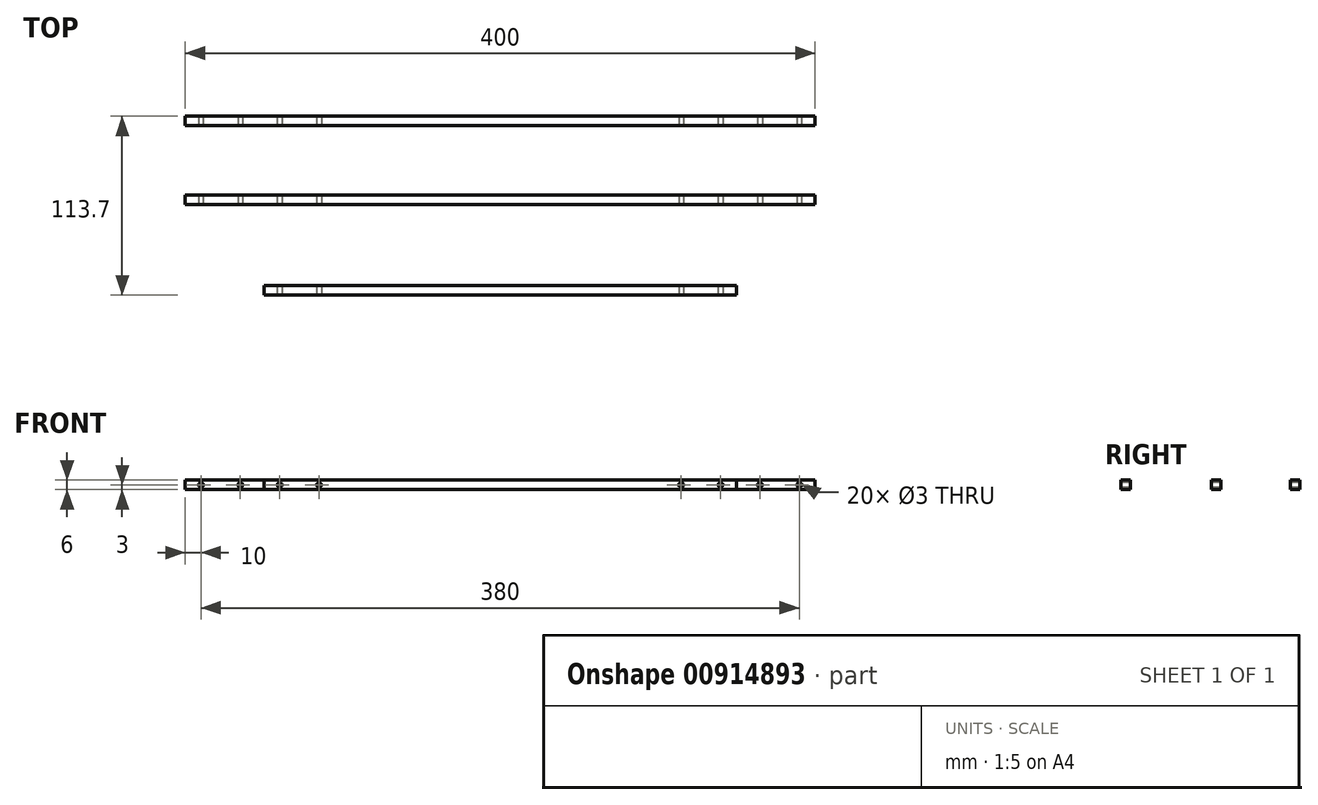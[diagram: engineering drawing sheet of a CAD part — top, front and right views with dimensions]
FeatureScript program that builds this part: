
annotation { "Feature Type Name" : "Feature", "Feature Type Description" : "" }
export const myFeature = defineFeature(function(context is Context, id is Id, definition is map)
    precondition{}
    {
        {
            var Q0;
            Q0=qCreatedBy(makeId("Top.planeOp"),FACE);
            var sketch = newSketch(context, id + "F0", { "sketchPlane" : qUnion([Q0])});
            skLineSegment(sketch, "E0.bottom", {"start": v(200, -3) * mm, "end": v(-200, -3) * mm});
            skLineSegment(sketch, "E0.top", {"start": v(200, 3) * mm, "end": v(-200, 3) * mm});
            skLineSegment(sketch, "E0.left", {"start": v(200, -3) * mm, "end": v(200, 3) * mm});
            skLineSegment(sketch, "E0.right", {"start": v(-200, -3) * mm, "end": v(-200, 3) * mm});
            skPoint(sketch, "E0.middle", {"position": v(0, 0) * mm});
            skLineSegment(sketch, "E1.bottom", {"start": v(150, -110.7) * mm, "end": v(-150, -110.7) * mm});
            skLineSegment(sketch, "E1.top", {"start": v(150, -104.7) * mm, "end": v(-150, -104.7) * mm});
            skLineSegment(sketch, "E1.left", {"start": v(150, -110.7) * mm, "end": v(150, -104.7) * mm});
            skLineSegment(sketch, "E1.right", {"start": v(-150, -110.7) * mm, "end": v(-150, -104.7) * mm});
            skPoint(sketch, "E1.middle", {"position": v(0, -107.7) * mm});
            skSolve(sketch);
        }
        {
            var Q0;
            Q0=makeQuery(id+"F0.imprint","IMPRINT",FACE,{"disambiguationData":[TD([[makeQuery(id+"F0.imprint","IMPRINT",EDGE,{"derivedFrom":sQuery(id+"F0.wireOp",EDGE,"E0.bottom")}),-1.0]])]});
            extrude(context, id + "F1", {"entities" : qUnion([Q0]), "depth" : 6 * mm, "offsetDistance" : 25 * mm});
        }
        {
            var Q0;
            Q0=qCreatedBy(makeId("Top.planeOp"),FACE);
            var sketch = newSketch(context, id + "F2", { "sketchPlane" : qUnion([Q0])});
            skLineSegment(sketch, "E2.bottom", {"start": v(200, -53) * mm, "end": v(-200, -53) * mm});
            skLineSegment(sketch, "E2.top", {"start": v(200, -47) * mm, "end": v(-200, -47) * mm});
            skLineSegment(sketch, "E2.left", {"start": v(200, -53) * mm, "end": v(200, -47) * mm});
            skLineSegment(sketch, "E2.right", {"start": v(-200, -53) * mm, "end": v(-200, -47) * mm});
            skPoint(sketch, "E2.middle", {"position": v(0, -50) * mm});
            skSolve(sketch);
        }
        {
            var Q0;
            Q0 = qSketchRegion(id + "F2", true);
            extrude(context, id + "F3", {"entities" : qUnion([Q0]), "depth" : 6 * mm, "offsetDistance" : 25 * mm});
        }
        {
            var Q0;
            Q0=makeQuery(id+"F1.opExtrude","SWEPT_FACE",FACE,{"disambiguationData":[OSD([sQuery(id+"F0.wireOp",EDGE,"E0.bottom")])]});
            var sketch = newSketch(context, id + "F4", { "sketchPlane" : qUnion([Q0])});
            skLineSegment(sketch, "E3", {"start": v(0, 24.85) * mm, "end": v(0, -23.8) * mm, "construction": true});
            skLineSegment(sketch, "E4", {"start": v(203.05, 3) * mm, "end": v(153.8, 3) * mm, "construction": true});
            skPoint(sketch, "E4.startSnap0", {"position": v(200, 3) * mm});
            skCircle(sketch, "E5", {"center": v(190, 3) * mm, "radius": 1.5 * mm});
            skCircle(sketch, "E6", {"center": v(165, 3) * mm, "radius": 1.5 * mm});
            skCircle(sketch, "E7.MirrorC", {"center": v(-190, 3) * mm, "radius": 1.5 * mm});
            skCircle(sketch, "E8.MirrorC", {"center": v(-165, 3) * mm, "radius": 1.5 * mm});
            skPoint(sketch, "E9.MirrorP", {"position": v(-200, 3) * mm});
            skLineSegment(sketch, "E10.MirrorCS", {"start": v(-203.05, 3) * mm, "end": v(-153.8, 3) * mm, "construction": true});
            skSolve(sketch);
        }
        {
            var Q0;
            Q0 = qSketchRegion(id + "F4", true);
            extrude(context, id + "F5", {"entities" : qUnion([Q0]), "operationType" : NewBodyOperationType.REMOVE, "endBound" : BoundingType.THROUGH_ALL, "oppositeDirection" : true, "depth" : 25 * mm, "offsetDistance" : 25 * mm});
        }
        {
            var Q0;
            Q0=makeQuery(id+"F3.opExtrude","SWEPT_FACE",FACE,{"disambiguationData":[OSD([sQuery(id+"F2.wireOp",EDGE,"E2.bottom")])]});
            var sketch = newSketch(context, id + "F6", { "sketchPlane" : qUnion([Q0])});
            skLineSegment(sketch, "E11", {"start": v(0, 27.32) * mm, "end": v(0, -16.64) * mm, "construction": true});
            skLineSegment(sketch, "E12", {"start": v(152.75, 3) * mm, "end": v(99.55, 3) * mm, "construction": true});
            skPoint(sketch, "E12.startSnap0", {"position": v(200, 3) * mm});
            skCircle(sketch, "E13", {"center": v(190, 3) * mm, "radius": 1.5 * mm});
            skCircle(sketch, "E14", {"center": v(165, 3) * mm, "radius": 1.5 * mm});
            skCircle(sketch, "E15.MirrorC", {"center": v(-190, 3) * mm, "radius": 1.5 * mm});
            skCircle(sketch, "E16.MirrorC", {"center": v(-165, 3) * mm, "radius": 1.5 * mm});
            skPoint(sketch, "E17.MirrorP", {"position": v(-200, 3) * mm});
            skLineSegment(sketch, "E18.MirrorCS", {"start": v(-152.75, 3) * mm, "end": v(-99.55, 3) * mm, "construction": true});
            skSolve(sketch);
        }
        {
            var Q0;
            Q0 = qSketchRegion(id + "F6", true);
            extrude(context, id + "F7", {"entities" : qUnion([Q0]), "operationType" : NewBodyOperationType.REMOVE, "endBound" : BoundingType.THROUGH_ALL, "oppositeDirection" : true, "depth" : 25 * mm, "offsetDistance" : 25 * mm});
        }
        {
            var Q0;
            Q0=makeQuery(id+"F0.imprint","IMPRINT",FACE,{"disambiguationData":[TD([[makeQuery(id+"F0.imprint","IMPRINT",EDGE,{"derivedFrom":sQuery(id+"F0.wireOp",EDGE,"E1.bottom")}),-1.0]])]});
            extrude(context, id + "F8", {"entities" : qUnion([Q0]), "depth" : 6 * mm, "offsetDistance" : 25 * mm});
        }
        {
            var Q0;
            Q0=makeQuery(id+"F8.opExtrude","SWEPT_FACE",FACE,{"disambiguationData":[OSD([sQuery(id+"F0.wireOp",EDGE,"E1.bottom")])]});
            var sketch = newSketch(context, id + "F9", { "sketchPlane" : qUnion([Q0])});
            skLineSegment(sketch, "E19", {"start": v(0, 10.88) * mm, "end": v(0, -9.9) * mm, "construction": true});
            skLineSegment(sketch, "E20", {"start": v(123.66, 3) * mm, "end": v(65.03, 3) * mm, "construction": true});
            skPoint(sketch, "E20.startSnap0", {"position": v(150, 3) * mm});
            skCircle(sketch, "E21", {"center": v(140, 3) * mm, "radius": 1.5 * mm});
            skCircle(sketch, "E22", {"center": v(115, 3) * mm, "radius": 1.5 * mm});
            skCircle(sketch, "E23.MirrorC", {"center": v(-115, 3) * mm, "radius": 1.5 * mm});
            skCircle(sketch, "E24.MirrorC", {"center": v(-140, 3) * mm, "radius": 1.5 * mm});
            skPoint(sketch, "E25.MirrorP", {"position": v(-150, 3) * mm});
            skSolve(sketch);
        }
        {
            var Q0;
            Q0 = qSketchRegion(id + "F9", true);
            extrude(context, id + "F10", {"entities" : qUnion([Q0]), "operationType" : NewBodyOperationType.REMOVE, "endBound" : BoundingType.THROUGH_ALL, "oppositeDirection" : true, "depth" : 25 * mm, "offsetDistance" : 25 * mm});
        }
    });
